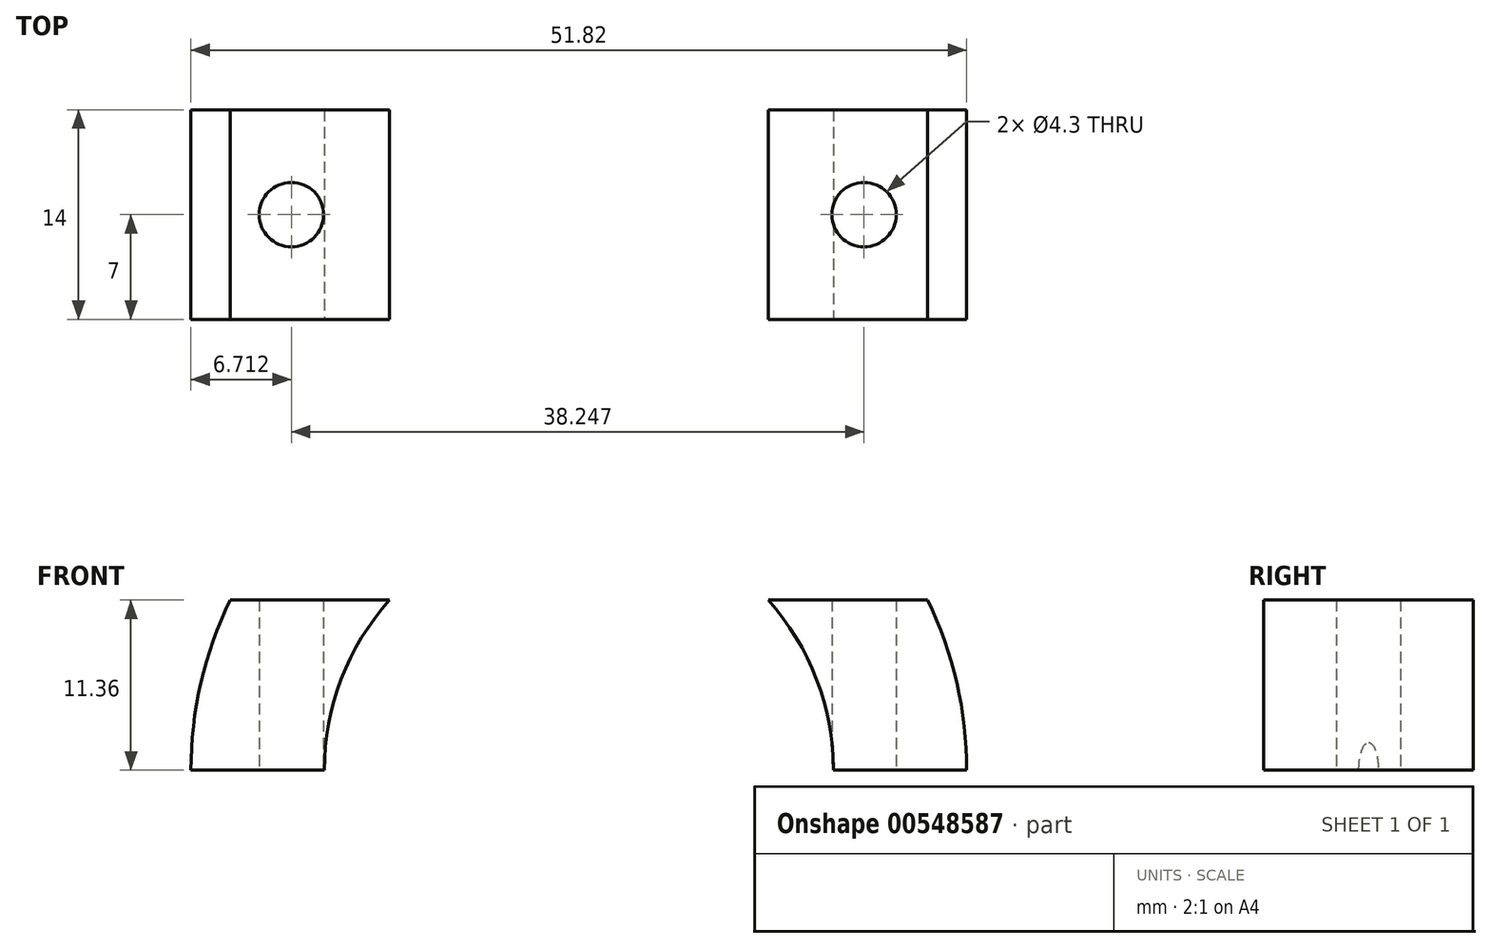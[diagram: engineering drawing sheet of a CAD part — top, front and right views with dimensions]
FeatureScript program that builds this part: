
annotation { "Feature Type Name" : "Feature", "Feature Type Description" : "" }
export const myFeature = defineFeature(function(context is Context, id is Id, definition is map)
    precondition{}
    {
        {
            var Q0;
            Q0=qCreatedBy(makeId("Front.planeOp"),FACE);
            var sketch = newSketch(context, id + "F0", { "sketchPlane" : qUnion([Q0])});
            skCircle(sketch, "E0", {"center": v(0, 0) * mm, "radius": 25.9 * mm});
            skSolve(sketch);
        }
        {
            var Q0;
            Q0=qSketchRegion(id+"F0",true);
            extrude(context, id + "F1", {"entities" : qUnion([Q0]), "depth" : 7 * mm, "offsetDistance" : 25 * mm, "hasSecondDirection" : true, "secondDirectionOppositeDirection" : true, "secondDirectionDepth" : 7 * mm});
        }
        {
            var Q0;
            Q0=qCreatedBy(makeId("Front.planeOp"),FACE);
            var sketch = newSketch(context, id + "F2", { "sketchPlane" : qUnion([Q0])});
            skCircle(sketch, "E1", {"center": v(0, 0) * mm, "radius": 17 * mm});
            skSolve(sketch);
        }
        {
            var Q0;
            Q0=qSketchRegion(id+"F2",true);
            extrude(context, id + "F3", {"entities" : qUnion([Q0]), "operationType" : NewBodyOperationType.REMOVE, "oppositeDirection" : true, "depth" : 7 * mm, "offsetDistance" : 25 * mm, "hasSecondDirection" : true, "secondDirectionOppositeDirection" : false, "secondDirectionDepth" : 7 * mm});
        }
        {
            var Q0;
            Q0=qCreatedBy(makeId("Top.planeOp"),FACE);
            var sketch = newSketch(context, id + "F4", { "sketchPlane" : qUnion([Q0])});
            skLineSegment(sketch, "E2.bottom", {"start": v(-62.72, 7) * mm, "end": v(62.72, 7) * mm});
            skLineSegment(sketch, "E2.top", {"start": v(-62.72, -7) * mm, "end": v(62.72, -7) * mm});
            skLineSegment(sketch, "E2.left", {"start": v(-62.72, 7) * mm, "end": v(-62.72, -7) * mm});
            skLineSegment(sketch, "E2.right", {"start": v(62.72, 7) * mm, "end": v(62.72, -7) * mm});
            skPoint(sketch, "E2.middle", {"position": v(0, 0) * mm});
            skSolve(sketch);
        }
        {
            var Q0;
            Q0=makeQuery(id+"F4.imprint","IMPRINT",FACE,{"disambiguationData":[TD([[makeQuery(id+"F4.imprint","IMPRINT",EDGE,{"derivedFrom":sQuery(id+"F4.wireOp",EDGE,"E2.bottom")}),-1.0]])]});
            var sketch = newSketch(context, id + "F5", { "sketchPlane" : qUnion([Q0])});
            skLineSegment(sketch, "E3.bottom", {"start": v(-15.9, 7) * mm, "end": v(-25.91, 7) * mm});
            skLineSegment(sketch, "E3.top", {"start": v(-15.9, -7) * mm, "end": v(-25.91, -7) * mm});
            skLineSegment(sketch, "E3.left", {"start": v(-15.9, 7) * mm, "end": v(-15.9, -7) * mm});
            skLineSegment(sketch, "E3.right", {"start": v(-25.91, 7) * mm, "end": v(-25.91, -7) * mm});
            skLineSegment(sketch, "E4.bottom", {"start": v(15.9, 7) * mm, "end": v(25.91, 7) * mm});
            skLineSegment(sketch, "E4.top", {"start": v(15.9, -7) * mm, "end": v(25.91, -7) * mm});
            skLineSegment(sketch, "E4.left", {"start": v(15.9, 7) * mm, "end": v(15.9, -7) * mm});
            skLineSegment(sketch, "E4.right", {"start": v(25.91, 7) * mm, "end": v(25.91, -7) * mm});
            skSolve(sketch);
        }
        {
            var Q0;
            Q0=qSketchRegion(id+"F5",true);
            extrude(context, id + "F6", {"entities" : qUnion([Q0]), "operationType" : NewBodyOperationType.ADD, "oppositeDirection" : true, "depth" : 20 * mm, "offsetDistance" : 25 * mm});
        }
        {
            var Q0;
            Q0=makeQuery(id+"F4.imprint","IMPRINT",FACE,{"disambiguationData":[TD([[makeQuery(id+"F4.imprint","IMPRINT",EDGE,{"derivedFrom":sQuery(id+"F4.wireOp",EDGE,"E2.bottom")}),-1.0]])]});
            var sketch = newSketch(context, id + "F7", { "sketchPlane" : qUnion([Q0])});
            skCircle(sketch, "E5", {"center": v(-19.2, 0) * mm, "radius": 2.15 * mm});
            skCircle(sketch, "E6", {"center": v(19.05, 0) * mm, "radius": 2.15 * mm});
            skSolve(sketch);
        }
        {
            var Q0;
            Q0=qSketchRegion(id+"F7",true);
            extrude(context, id + "F8", {"entities" : qUnion([Q0]), "operationType" : NewBodyOperationType.REMOVE, "depth" : 30 * mm, "offsetDistance" : 25 * mm, "hasSecondDirection" : true, "secondDirectionOppositeDirection" : true, "secondDirectionDepth" : 30 * mm});
        }
        {
            var Q0;
            Q0=makeQuery(id+"F6.opExtrude","CAP_FACE",FACE,{"disambiguationData":[OSD([sQuery(id+"F5.wireOp",EDGE,"E3.bottom"),sQuery(id+"F5.wireOp",EDGE,"E3.top"),sQuery(id+"F5.wireOp",EDGE,"E3.left"),sQuery(id+"F5.wireOp",EDGE,"E3.right")])],"isStart":false});
            var sketch = newSketch(context, id + "F9", { "sketchPlane" : qUnion([Q0])});
            skLineSegment(sketch, "E7.bottom", {"start": v(-25.91, -7) * mm, "end": v(-11.9, -7) * mm});
            skLineSegment(sketch, "E7.top", {"start": v(-25.91, 7) * mm, "end": v(-11.91, 7) * mm});
            skLineSegment(sketch, "E7.left", {"start": v(-25.91, -7) * mm, "end": v(-25.91, 7) * mm});
            skLineSegment(sketch, "E7.right", {"start": v(-11.9, -7) * mm, "end": v(-11.91, 7) * mm});
            skLineSegment(sketch, "E8.bottom", {"start": v(25.91, -7) * mm, "end": v(11.91, -7) * mm});
            skLineSegment(sketch, "E8.top", {"start": v(25.91, 7) * mm, "end": v(11.9, 7) * mm});
            skLineSegment(sketch, "E8.left", {"start": v(25.91, -7) * mm, "end": v(25.91, 7) * mm});
            skLineSegment(sketch, "E8.right", {"start": v(11.91, -7) * mm, "end": v(11.9, 7) * mm});
            skSolve(sketch);
        }
        {
            var Q0;
            Q0=qSketchRegion(id+"F9",true);
            extrude(context, id + "F10", {"entities" : qUnion([Q0]), "operationType" : NewBodyOperationType.REMOVE, "depth" : 3 * mm, "offsetDistance" : 25 * mm});
        }
        {
            var Q0;
            Q0=makeQuery(id+"F6.boolean.opBoolean","MERGE",FACE,{"derivedFrom":[makeQuery(id+"F1.opExtrude","CAP_FACE",FACE,{"disambiguationData":[OSD([sQuery(id+"F0.wireOp",EDGE,"E0")])],"isStart":false}),makeQuery(id+"F6.opExtrude","SWEPT_FACE",FACE,{"disambiguationData":[OSD([sQuery(id+"F5.wireOp",EDGE,"E3.top")])]}),makeQuery(id+"F6.opExtrude","SWEPT_FACE",FACE,{"disambiguationData":[OSD([sQuery(id+"F5.wireOp",EDGE,"E4.top")])]})]});
            var sketch = newSketch(context, id + "F11", { "sketchPlane" : qUnion([Q0])});
            skLineSegment(sketch, "E9.bottom", {"start": v(36.26, 0) * mm, "end": v(51.82, 0) * mm});
            skLineSegment(sketch, "E9.top", {"start": v(36.26, 11.36) * mm, "end": v(51.82, 11.36) * mm});
            skLineSegment(sketch, "E9.left", {"start": v(36.26, 0) * mm, "end": v(36.26, 11.36) * mm});
            skLineSegment(sketch, "E9.right", {"start": v(51.82, 0) * mm, "end": v(51.82, 11.36) * mm});
            skSolve(sketch);
        }
        {
            var Q0;
            Q0=makeQuery(id+"F6.boolean.opBoolean","MERGE",FACE,{"derivedFrom":[makeQuery(id+"F1.opExtrude","CAP_FACE",FACE,{"disambiguationData":[OSD([sQuery(id+"F0.wireOp",EDGE,"E0")])],"isStart":true}),makeQuery(id+"F6.opExtrude","SWEPT_FACE",FACE,{"disambiguationData":[OSD([sQuery(id+"F5.wireOp",EDGE,"E3.bottom")])]}),makeQuery(id+"F6.opExtrude","SWEPT_FACE",FACE,{"disambiguationData":[OSD([sQuery(id+"F5.wireOp",EDGE,"E4.bottom")])]})]});
            var sketch = newSketch(context, id + "F12", { "sketchPlane" : qUnion([Q0])});
            skLineSegment(sketch, "E10", {"start": v(-48.16, 0) * mm, "end": v(-48.16, 11.36) * mm});
            skSolve(sketch);
        }
        {
            var Q0;
            Q0=sQuery(id+"F11.wireOp",VERTEX,"E9.right.end");
            var Q1;
            Q1=sQuery(id+"F12.wireOp",VERTEX,"E10.end");
            var Q2;
            Q2=sQuery(id+"F11.wireOp",VERTEX,"E9.left.end");
            cPlane(context, id + "F13", {"entities" : qUnion([Q0, Q1, Q2]), "cplaneType" : CPlaneType.THREE_POINT, "offset" : 25 * mm, "width" : 150 * mm, "height" : 150 * mm});
        }
        {
            var Q0;
            Q0=qCreatedBy(id+"F13.planeOp",FACE);
            var sketch = newSketch(context, id + "F14", { "sketchPlane" : qUnion([Q0])});
            skLineSegment(sketch, "E11.bottom", {"start": v(70.32, 38.8) * mm, "end": v(-52.4, 38.8) * mm});
            skLineSegment(sketch, "E11.top", {"start": v(70.32, -46.16) * mm, "end": v(-52.4, -46.16) * mm});
            skLineSegment(sketch, "E11.left", {"start": v(70.32, 38.8) * mm, "end": v(70.32, -46.16) * mm});
            skLineSegment(sketch, "E11.right", {"start": v(-52.4, 38.8) * mm, "end": v(-52.4, -46.16) * mm});
            skSolve(sketch);
        }
        {
            var Q0;
            Q0=qSketchRegion(id+"F14",true);
            extrude(context, id + "F15", {"entities" : qUnion([Q0]), "operationType" : NewBodyOperationType.REMOVE, "oppositeDirection" : true, "depth" : 18 * mm, "offsetDistance" : 25 * mm});
        }
        {
            var Q0;
            Q0=makeQuery(id+"F4.imprint","IMPRINT",FACE,{"disambiguationData":[TD([[makeQuery(id+"F4.imprint","IMPRINT",EDGE,{"derivedFrom":sQuery(id+"F4.wireOp",EDGE,"E2.bottom")}),-1.0]])]});
            var sketch = newSketch(context, id + "F16", { "sketchPlane" : qUnion([Q0])});
            skLineSegment(sketch, "E12.bottom", {"start": v(-34.96, 23.73) * mm, "end": v(35.63, 23.73) * mm});
            skLineSegment(sketch, "E12.top", {"start": v(-34.96, -22.51) * mm, "end": v(35.63, -22.51) * mm});
            skLineSegment(sketch, "E12.left", {"start": v(-34.96, 23.73) * mm, "end": v(-34.96, -22.51) * mm});
            skLineSegment(sketch, "E12.right", {"start": v(35.63, 23.73) * mm, "end": v(35.63, -22.51) * mm});
            skSolve(sketch);
        }
        {
            var Q0;
            Q0 = qSketchRegion(id + "F16", true);
            extrude(context, id + "F17", {"entities" : qUnion([Q0]), "operationType" : NewBodyOperationType.REMOVE, "oppositeDirection" : true, "depth" : 30 * mm, "offsetDistance" : 25 * mm});
        }
    });
